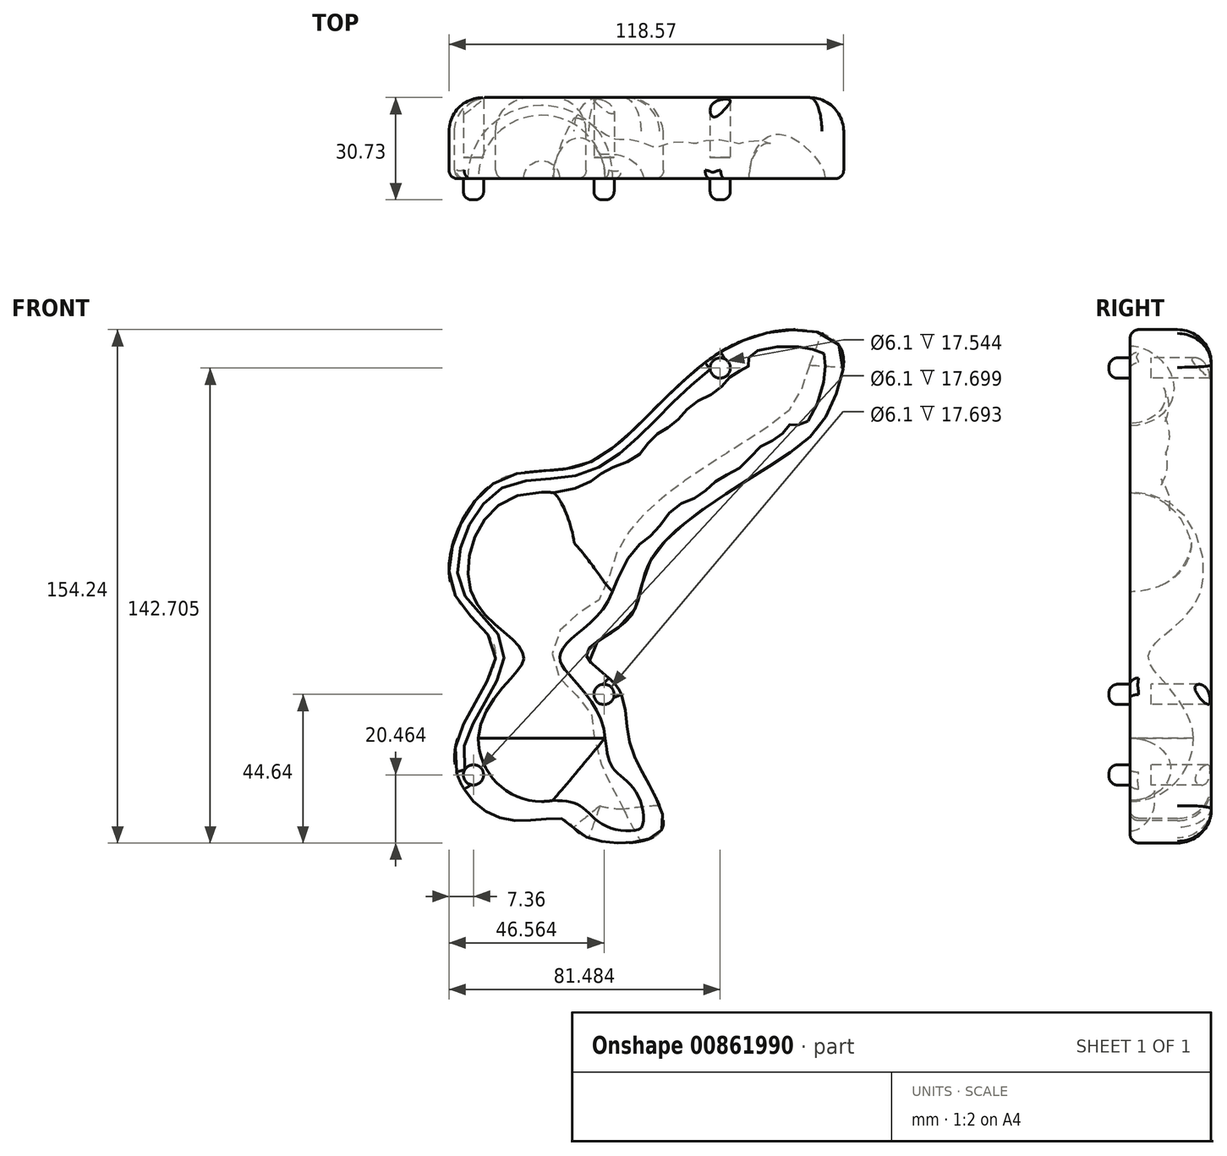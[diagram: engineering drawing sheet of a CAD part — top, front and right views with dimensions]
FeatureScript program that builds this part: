
annotation { "Feature Type Name" : "Feature", "Feature Type Description" : "" }
export const myFeature = defineFeature(function(context is Context, id is Id, definition is map)
    precondition{}
    {
        {
            var Q0;
            Q0=qCreatedBy(makeId("Front.planeOp"),FACE);
            var sketch = newSketch(context, id + "F0", { "sketchPlane" : qUnion([Q0])});
            skArc(sketch, "E0", {"start": v(0, -69.85) * mm, "mid": v(13.47, -64.27) * mm, "end": v(19.05, -50.8) * mm});
            skFitSpline(sketch, "E1", {"points": [v(-0.01, 23.13) * mm, v(21.58, -5.45) * mm, v(9.13, -20.77) * mm, v(5.4, -26.76) * mm, v(8.89, -32.47) * mm, v(19.05, -50.8) * mm], "startDerivative": vector(184.16, 1) * mm, "endDerivative": vector(2.36, -95.96) * mm});
            skLineSegment(sketch, "E2", {"start": v(0, 23.13) * mm, "end": v(0, -69.85) * mm});
            skSolve(sketch);
        }
        {
            var Q0;
            Q0=makeQuery(id+"F0.imprint","IMPRINT",FACE,{"disambiguationData":[TD([[makeQuery(id+"F0.imprint","IMPRINT",EDGE,{"derivedFrom":sQuery(id+"F0.wireOp",EDGE,"E0")}),1.0]])]});
            var Q1;
            Q1=sQuery(id+"F0.wireOp",EDGE,"E2");
            revolve(context, id + "F1", {"surfaceOperationType" : NewSurfaceOperationType.NEW, "entities" : qUnion([Q0]), "axis" : qUnion([Q1]), "revolveType" : RevolveType.FULL});
        }
        {
            var Q0;
            Q0=qCreatedBy(makeId("Front.planeOp"),FACE);
            var sketch = newSketch(context, id + "F2", { "sketchPlane" : qUnion([Q0])});
            skLineSegment(sketch, "E3", {"start": v(0, -50.6) * mm, "end": v(29.97, -77.77) * mm});
            skFitSpline(sketch, "E4", {"points": [v(19.06, -50.8) * mm, v(21.67, -60.14) * mm, v(28.3, -66.98) * mm, v(29.97, -77.77) * mm, v(0, -69.87) * mm], "startDerivative": vector(7.5, -65.65) * mm, "endDerivative": vector(-157.41, 58.8) * mm});
            skLineSegment(sketch, "E5", {"start": v(19.06, -50.8) * mm, "end": v(0, -50.6) * mm});
            skSolve(sketch);
        }
        {
            var Q0;
            Q0=makeQuery(id+"F2.imprint","IMPRINT",FACE,{"disambiguationData":[TD([[makeQuery(id+"F2.imprint","IMPRINT",EDGE,{"derivedFrom":sQuery(id+"F2.wireOp",EDGE,"E3")}),1.0]])]});
            var Q1;
            Q1=sQuery(id+"F2.wireOp",EDGE,"E3");
            revolve(context, id + "F3", {"operationType" : NewBodyOperationType.ADD, "surfaceOperationType" : NewSurfaceOperationType.NEW, "entities" : qUnion([Q0]), "axis" : qUnion([Q1]), "revolveType" : RevolveType.FULL});
        }
        {
            var Q0;
            Q0=qCreatedBy(makeId("Front.planeOp"),FACE);
            var sketch = newSketch(context, id + "F4", { "sketchPlane" : qUnion([Q0])});
            skLineSegment(sketch, "E6", {"start": v(0, 0) * mm, "end": v(84.83, 64.67) * mm});
            skFitSpline(sketch, "E7", {"points": [v(84.83, 64.67) * mm, v(84.83, 56.57) * mm, v(78.49, 43.23) * mm, v(75.2, 43.78) * mm, v(71.9, 40.23) * mm, v(65.99, 36.92) * mm, v(59.6, 30.54) * mm, v(52.75, 26.75) * mm, v(47.3, 22.02) * mm, v(39.98, 18.48) * mm, v(33.76, 10.84) * mm, v(27.55, 5.5) * mm, v(21.16, -6.9) * mm, v(0, 0) * mm], "startDerivative": vector(13.16, -101.21) * mm, "endDerivative": vector(-606.42, -29.56) * mm});
            skSolve(sketch);
        }
        {
            var Q0;
            Q0=makeQuery(id+"F4.imprint","IMPRINT",FACE,{"disambiguationData":[TD([[makeQuery(id+"F4.imprint","IMPRINT",EDGE,{"derivedFrom":sQuery(id+"F4.wireOp",EDGE,"E6")}),-1.0]])]});
            var Q1;
            Q1=sQuery(id+"F4.wireOp",EDGE,"E6");
            revolve(context, id + "F5", {"operationType" : NewBodyOperationType.ADD, "surfaceOperationType" : NewSurfaceOperationType.NEW, "entities" : qUnion([Q0]), "axis" : qUnion([Q1]), "revolveType" : RevolveType.FULL});
        }
        {
            var Q0;
            Q0=qCreatedBy(makeId("Front.planeOp"),FACE);
            var sketch = newSketch(context, id + "F6", { "sketchPlane" : qUnion([Q0])});
            skFitSpline(sketch, "E8", {"points": [v(-13.87, -24.9) * mm, v(-27.09, -5.5) * mm, v(-13.7, 26.23) * mm, v(14.1, 31.94) * mm, v(56.55, 66.82) * mm, v(89.32, 67.24) * mm, v(86.8, 48.75) * mm, v(76.19, 36.08) * mm, v(33.66, 4.19) * mm, v(26.16, -14.89) * mm, v(13.34, -25.52) * mm, v(22.72, -35.53) * mm, v(27.1, -54.29) * mm, v(35.85, -78.68) * mm, v(12.71, -80.24) * mm, v(6.77, -75.24) * mm, v(-11.99, -74.92) * mm, v(-26.06, -54.6) * mm, v(-13.87, -24.9) * mm]});
            skCircle(sketch, "E9", {"center": v(18.7, -37.69) * mm, "radius": 3.05 * mm});
            skCircle(sketch, "E10", {"center": v(-20.5, -61.87) * mm, "radius": 3.05 * mm});
            skCircle(sketch, "E11", {"center": v(53.62, 60.37) * mm, "radius": 3.05 * mm});
            skSolve(sketch);
        }
        {
            var Q0;
            Q0=makeQuery(id+"F6.imprint","IMPRINT",FACE,{"disambiguationData":[TD([[makeQuery(id+"F6.imprint","IMPRINT",EDGE,{"derivedFrom":sQuery(id+"F6.wireOp",EDGE,"E8")}),-1.0]])]});
            extrude(context, id + "F7", {"entities" : qUnion([Q0]), "oppositeDirection" : true, "depth" : 24.38 * mm, "offsetDistance" : 25.4 * mm});
        }
        {
            var Q0;
            Q0=makeQuery(id+"F6.imprint","IMPRINT",FACE,{"disambiguationData":[TD([[makeQuery(id+"F6.imprint","IMPRINT",EDGE,{"derivedFrom":sQuery(id+"F6.wireOp",EDGE,"E11")}),1.0]])]});
            var Q1;
            Q1=makeQuery(id+"F6.imprint","IMPRINT",FACE,{"disambiguationData":[TD([[makeQuery(id+"F6.imprint","IMPRINT",EDGE,{"derivedFrom":sQuery(id+"F6.wireOp",EDGE,"E9")}),1.0]])]});
            var Q2;
            Q2=makeQuery(id+"F6.imprint","IMPRINT",FACE,{"disambiguationData":[TD([[makeQuery(id+"F6.imprint","IMPRINT",EDGE,{"derivedFrom":sQuery(id+"F6.wireOp",EDGE,"E10")}),1.0]])]});
            extrude(context, id + "F8", {"entities" : qUnion([Q0, Q1, Q2]), "operationType" : NewBodyOperationType.ADD, "endBound" : BoundingType.SYMMETRIC, "depth" : 12.7 * mm, "offsetDistance" : 25.4 * mm});
        }
        {
            var Q0;
            Q0=makeQuery(id+"F7.opExtrude","CAP_EDGE",EDGE,{"disambiguationData":[OSD([sQuery(id+"F6.wireOp",EDGE,"E8")])],"isStart":true});
            var Q1;
            Q1=makeQuery(id+"F8.opExtrude","CAP_EDGE",EDGE,{"disambiguationData":[OSD([sQuery(id+"F6.wireOp",EDGE,"E9")])],"isStart":false});
            var Q2;
            Q2=makeQuery(id+"F8.opExtrude","CAP_EDGE",EDGE,{"disambiguationData":[OSD([sQuery(id+"F6.wireOp",EDGE,"E11")])],"isStart":false});
            var Q3;
            Q3=makeQuery(id+"F8.opExtrude","CAP_EDGE",EDGE,{"disambiguationData":[OSD([sQuery(id+"F6.wireOp",EDGE,"E10")])],"isStart":false});
            fillet(context, id + "F9", {"entities" : qUnion([Q0, Q1, Q2, Q3]), "radius" : 2.54 * mm, "tangentPropagation" : true, "allowEdgeOverflow" : false});
        }
        {
            var Q0;
            Q0=makeQuery(id+"F7.opExtrude","CAP_EDGE",EDGE,{"disambiguationData":[OSD([sQuery(id+"F6.wireOp",EDGE,"E8")])],"isStart":false});
            fillet(context, id + "F10", {"entities" : qUnion([Q0]), "radius" : 10.16 * mm, "tangentPropagation" : true, "allowEdgeOverflow" : false});
        }
        {
            var Q0;
            Q0=makeQuery(id+"F1.opRevolve","SWEPT_BODY",BODY,{"disambiguationData":[OSD([sQuery(id+"F0.wireOp",EDGE,"E0"),sQuery(id+"F0.wireOp",EDGE,"E1"),sQuery(id+"F0.wireOp",EDGE,"E2")])]});
            var Q1;
            Q1=makeQuery(id+"F7.opExtrude","SWEPT_BODY",BODY,{"disambiguationData":[OSD([sQuery(id+"F6.wireOp",EDGE,"E8"),sQuery(id+"F6.wireOp",EDGE,"E9"),sQuery(id+"F6.wireOp",EDGE,"E10"),sQuery(id+"F6.wireOp",EDGE,"E11")])]});
            booleanBodies(context, id + "F11", {"operationType" : BooleanOperationType.SUBTRACTION, "tools" : qUnion([Q0]), "targets" : qUnion([Q1])});
        }
    });
